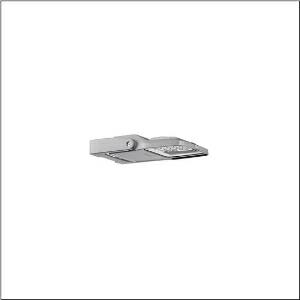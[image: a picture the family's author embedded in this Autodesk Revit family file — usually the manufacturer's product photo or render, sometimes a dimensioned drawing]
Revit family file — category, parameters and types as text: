
# Revit family: floodlight_fl_21_micro___pl64_5xa7761a4e2a_0330
name_source: partatom
category: Lighting Fixtures
units: mm (PartAtom-declared; Revit-internal decimal feet)

## family parameters
Cut with Voids When Loaded = No
Host = Face
Light Source = No
Part Type = Normal
Room Calculation Point = No
Round Connector Dimension = Use Diameter
Shared = No

## types (1)
- --- (1 x LED, 2980 lm, 23.1 W, 4000K)
    Apparent Load = 23 VA
    CIE Flux Codes = 28 80 98 100 100
    Color Rendering = 70
    Color Temperature = 4000K
    Default Elevation = 1800 mm
    Description = Floodlight FL 21 micro, floodlight, primary light control with lens, of PMMA, primary optical cover: protective disc, of toughened safety glass, transparent, light distribution: PL64, light emission: direct distribution, installation type: surface-mounted, LED, High Power LED, rated luminous flux: 2.980lm, luminous efficacy: 129lm/W, light colour: 740, colour temperature: 4000K, control gear: ECG iQ, control: optimised constant luminous flux control (CLO 2.0), Desk-Remote (wireless, voltage-free reading and setting of iQ features in the workshop via application-optimized NFC function/RFID function), Light-Fading, Smart-Wire, Night-Set, Lumen-Switch, Temp-Guard, Auto-Match, with terminal, 6-pole, mains connection: 220..240V, AC, 50/60Hz, start of lifetime: 23W, end of lifetime: 24W, reduction: 11W, luminaire housing, of diecast aluminium, powder-coated, Siteco® metallic grey (DB 702S), corrosivity category C5 according to DIN EN ISO 12944, design bracket, of diecast aluminium, powder-coated, Siteco® metallic grey (DB 702S), protection rating (complete): IP66, insulation class (complete): insulation class II (safety insulation), certification: CE, protection symbol: D, impact resistance: IK07, permissible operating ambient temperature: -40..+40°C, permissible operating ambient temperature for outdoor applications: -40..+50°C, standard: DIN EN 12944, packaging unit: 1 piece

Light Distribution: PL64
    Height = 65 mm
    Lamp = 1 x LED
    Lamp Light Flux = 2980 lm
    Lamp Power = 23.1 W
    Lamp count = 1
    Length = 312 mm
    Luminous efficacy = 129 lm/W
    Manufacturer = Siteco
    ModVariant = No
    Model = 5XA7761A4E2A
    Number of Poles = 1
    OnlyDefault = Yes
    Power Factor = 1
    Product Name = Floodlight FL 21 micro | PL64
    Product group = floodlight | pylon top
    ProductGroupID = 6101
    Protection Class = Protection class II
    Protection Degree = IP 66
    RLX_Detail_Level = 1
    RlxData = <blob elided: 97133 chars, md5=33dfbde6>
    Socket = socket
    Standby Power = 0 W
    System Light Flux = 2980 lm
    System Power = 23 W
    Type Comments = factory setting: luminous flux: 100 % | dim-lin: 254 | 455 mA
    Type Image = l_1006878.jpg
    URL = http://relux.com
    VarID = @adj_094347
    Voltage = 0 V
    Weight = 0.00 kg
    Width = 230 mm

## geometry (parser evidence)
native form markers: Blend x4, Sweep x13
no freeform markers — native parametric forms only
